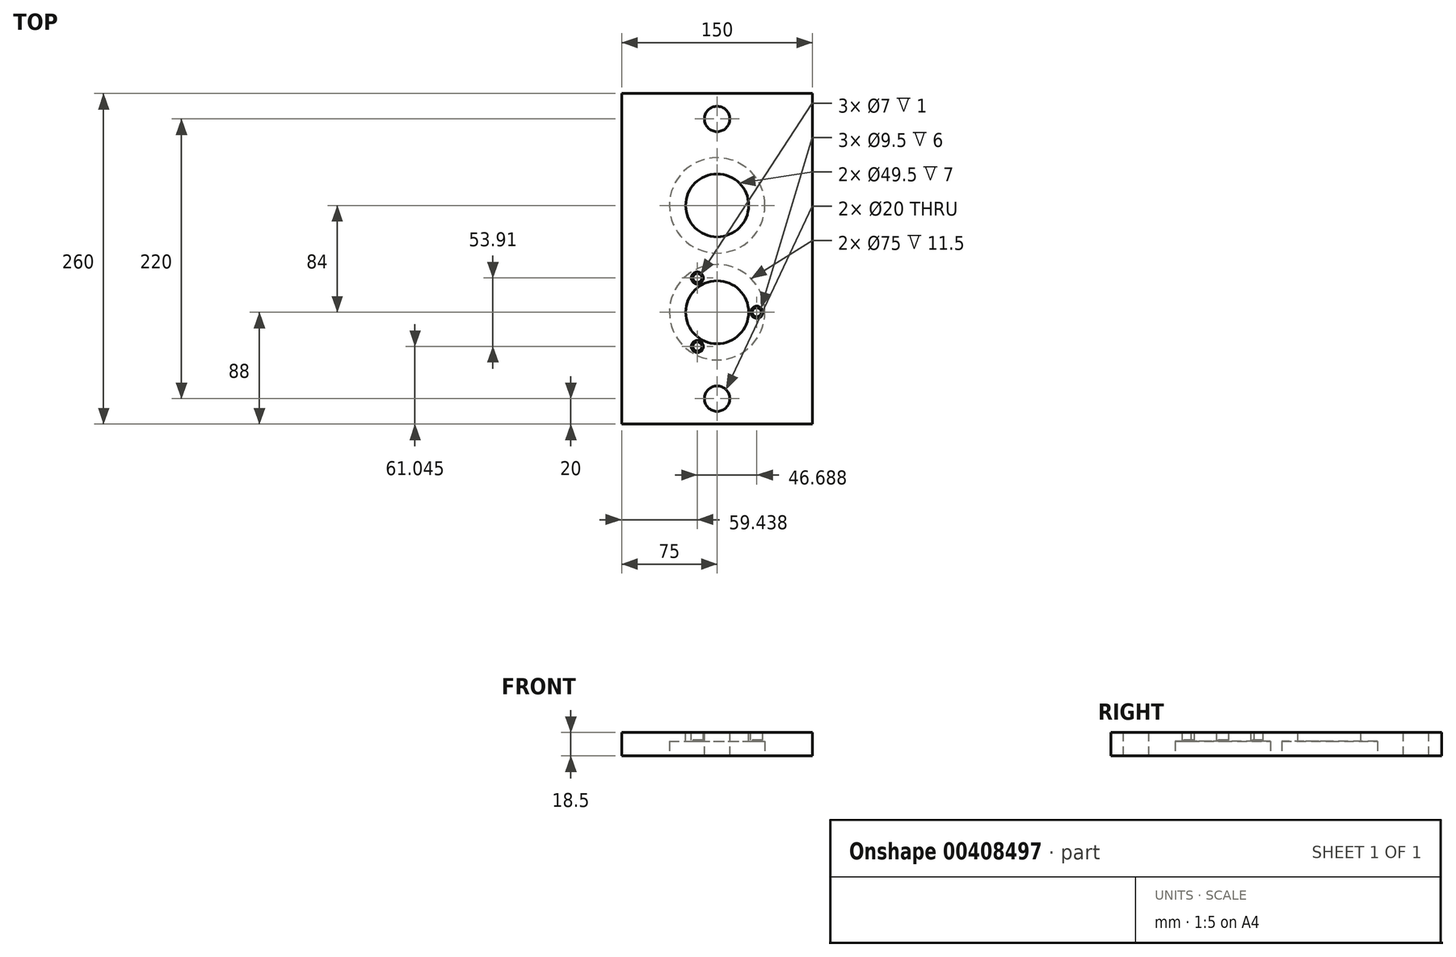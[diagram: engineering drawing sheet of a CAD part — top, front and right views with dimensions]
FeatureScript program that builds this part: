
annotation { "Feature Type Name" : "Feature", "Feature Type Description" : "" }
export const myFeature = defineFeature(function(context is Context, id is Id, definition is map)
    precondition{}
    {
        {
            var Q0;
            Q0=qCreatedBy(makeId("Top.planeOp"),FACE);
            var sketch = newSketch(context, id + "F0", { "sketchPlane" : qUnion([Q0])});
            skLineSegment(sketch, "E0", {"start": v(0, 0) * mm, "end": v(150, 0) * mm});
            skLineSegment(sketch, "E1", {"start": v(150, 0) * mm, "end": v(150, 260) * mm});
            skLineSegment(sketch, "E2", {"start": v(150, 260) * mm, "end": v(0, 260) * mm});
            skLineSegment(sketch, "E3", {"start": v(0, 260) * mm, "end": v(0, 0) * mm});
            skSolve(sketch);
        }
        {
            var Q0;
            Q0 = qSketchRegion(id + "F0", true);
            extrude(context, id + "F1", {"entities" : qUnion([Q0]), "depth" : 18.5 * mm});
        }
        {
            var Q0;
            Q0=makeQuery(id+"F1.opExtrude","CAP_FACE",FACE,{"disambiguationData":[OSD([sQuery(id+"F0.wireOp",EDGE,"E0"),sQuery(id+"F0.wireOp",EDGE,"E1"),sQuery(id+"F0.wireOp",EDGE,"E2"),sQuery(id+"F0.wireOp",EDGE,"E3")])],"isStart":false});
            var sketch = newSketch(context, id + "F2", { "sketchPlane" : qUnion([Q0])});
            skCircle(sketch, "E4", {"center": v(75, 240) * mm, "radius": 10 * mm});
            skCircle(sketch, "E5", {"center": v(75, 20) * mm, "radius": 10 * mm});
            skPoint(sketch, "E6.orphan", {"position": v(75, 0) * mm});
            skPoint(sketch, "E7.orphan", {"position": v(75, 260) * mm});
            skSolve(sketch);
        }
        {
            var Q0;
            Q0 = qSketchRegion(id + "F2", true);
            extrude(context, id + "F3", {"entities" : qUnion([Q0]), "operationType" : NewBodyOperationType.REMOVE, "oppositeDirection" : true, "depth" : 25.4 * mm});
        }
        {
            var Q0;
            Q0=makeQuery(id+"F1.opExtrude","CAP_FACE",FACE,{"disambiguationData":[OSD([sQuery(id+"F0.wireOp",EDGE,"E0"),sQuery(id+"F0.wireOp",EDGE,"E1"),sQuery(id+"F0.wireOp",EDGE,"E2"),sQuery(id+"F0.wireOp",EDGE,"E3")])],"isStart":false});
            var sketch = newSketch(context, id + "F4", { "sketchPlane" : qUnion([Q0])});
            skLineSegment(sketch, "E8", {"start": v(75, 260) * mm, "end": v(75, 260) * mm});
            skCircle(sketch, "E9", {"center": v(75, 172) * mm, "radius": 24.75 * mm});
            skCircle(sketch, "E10", {"center": v(75, 88) * mm, "radius": 24.75 * mm});
            skPoint(sketch, "E11.end.orphan", {"position": v(75, 0) * mm});
            skSolve(sketch);
        }
        {
            var Q0;
            Q0 = qSketchRegion(id + "F4", true);
            extrude(context, id + "F5", {"entities" : qUnion([Q0]), "operationType" : NewBodyOperationType.REMOVE, "oppositeDirection" : true, "depth" : 25.4 * mm});
        }
        {
            var Q0;
            Q0=makeQuery(id+"F1.opExtrude","CAP_FACE",FACE,{"disambiguationData":[OSD([sQuery(id+"F0.wireOp",EDGE,"E0"),sQuery(id+"F0.wireOp",EDGE,"E1"),sQuery(id+"F0.wireOp",EDGE,"E2"),sQuery(id+"F0.wireOp",EDGE,"E3")])],"isStart":true});
            var sketch = newSketch(context, id + "F6", { "sketchPlane" : qUnion([Q0])});
            skCircle(sketch, "E12", {"center": v(75, -88) * mm, "radius": 37.5 * mm});
            skCircle(sketch, "E13", {"center": v(75, -172) * mm, "radius": 37.5 * mm});
            skSolve(sketch);
        }
        {
            var Q0;
            Q0 = qSketchRegion(id + "F6", true);
            extrude(context, id + "F7", {"entities" : qUnion([Q0]), "operationType" : NewBodyOperationType.REMOVE, "oppositeDirection" : true, "depth" : 11.5 * mm});
        }
        {
            var Q0;
            Q0=makeQuery(id+"F7.boolean.opBoolean","COPY",FACE,{"derivedFrom":makeQuery(id+"F7.opExtrude","CAP_FACE",FACE,{"disambiguationData":[OSD([sQuery(id+"F6.wireOp",EDGE,"E12")])],"isStart":false})});
            var sketch = newSketch(context, id + "F8", { "sketchPlane" : qUnion([Q0])});
            skCircle(sketch, "E14", {"center": v(106.12, -88) * mm, "radius": 3.5 * mm});
            skPoint(sketch, "E15.trimOffspring.end.orphan", {"position": v(112.5, -88) * mm});
            skPoint(sketch, "E16.start.orphan", {"position": v(99.75, -88) * mm});
            skPoint(sketch, "E17.center.orphan", {"position": v(75, -88) * mm});
            skCircle(sketch, "E18.1.0", {"center": v(59.44, -61.04) * mm, "radius": 3.5 * mm});
            skCircle(sketch, "E18.2.0", {"center": v(59.44, -114.96) * mm, "radius": 3.5 * mm});
            skSolve(sketch);
        }
        {
            var Q0;
            Q0=makeQuery(id+"F8.imprint","IMPRINT",FACE,{"disambiguationData":[TD([[makeQuery(id+"F8.imprint","IMPRINT",EDGE,{"derivedFrom":sQuery(id+"F8.wireOp",EDGE,"E14")}),1.0]])]});
            var Q1;
            Q1=makeQuery(id+"F8.imprint","IMPRINT",FACE,{"disambiguationData":[TD([[makeQuery(id+"F8.imprint","IMPRINT",EDGE,{"derivedFrom":sQuery(id+"F8.wireOp",EDGE,"E18.1.0")}),1.0]])]});
            var Q2;
            Q2=makeQuery(id+"F8.imprint","IMPRINT",FACE,{"disambiguationData":[TD([[makeQuery(id+"F8.imprint","IMPRINT",EDGE,{"derivedFrom":sQuery(id+"F8.wireOp",EDGE,"E18.2.0")}),1.0]])]});
            extrude(context, id + "F9", {"entities" : qUnion([Q0, Q1, Q2]), "operationType" : NewBodyOperationType.REMOVE, "oppositeDirection" : true, "depth" : 25.4 * mm});
        }
        {
            var Q0;
            Q0=makeQuery(id+"F1.opExtrude","CAP_FACE",FACE,{"disambiguationData":[OSD([sQuery(id+"F0.wireOp",EDGE,"E0"),sQuery(id+"F0.wireOp",EDGE,"E1"),sQuery(id+"F0.wireOp",EDGE,"E2"),sQuery(id+"F0.wireOp",EDGE,"E3")])],"isStart":false});
            var sketch = newSketch(context, id + "F10", { "sketchPlane" : qUnion([Q0])});
            skCircle(sketch, "E19", {"center": v(106.12, 88) * mm, "radius": 4.75 * mm});
            skCircle(sketch, "E20", {"center": v(59.44, 114.96) * mm, "radius": 4.75 * mm});
            skCircle(sketch, "E21", {"center": v(59.44, 61.04) * mm, "radius": 4.75 * mm});
            skSolve(sketch);
        }
        {
            var Q0;
            Q0=makeQuery(id+"F10.imprint","IMPRINT",FACE,{"disambiguationData":[TD([[makeQuery(id+"F10.imprint","IMPRINT",EDGE,{"derivedFrom":sQuery(id+"F10.wireOp",EDGE,"E21")}),1.0]])]});
            var Q1;
            Q1=makeQuery(id+"F10.imprint","IMPRINT",FACE,{"disambiguationData":[TD([[makeQuery(id+"F10.imprint","IMPRINT",EDGE,{"derivedFrom":sQuery(id+"F10.wireOp",EDGE,"E20")}),1.0]])]});
            var Q2;
            Q2=makeQuery(id+"F10.imprint","IMPRINT",FACE,{"disambiguationData":[TD([[makeQuery(id+"F10.imprint","IMPRINT",EDGE,{"derivedFrom":sQuery(id+"F10.wireOp",EDGE,"E19")}),1.0]])]});
            extrude(context, id + "F11", {"entities" : qUnion([Q0, Q1, Q2]), "operationType" : NewBodyOperationType.REMOVE, "oppositeDirection" : true, "depth" : 6 * mm});
        }
    });
